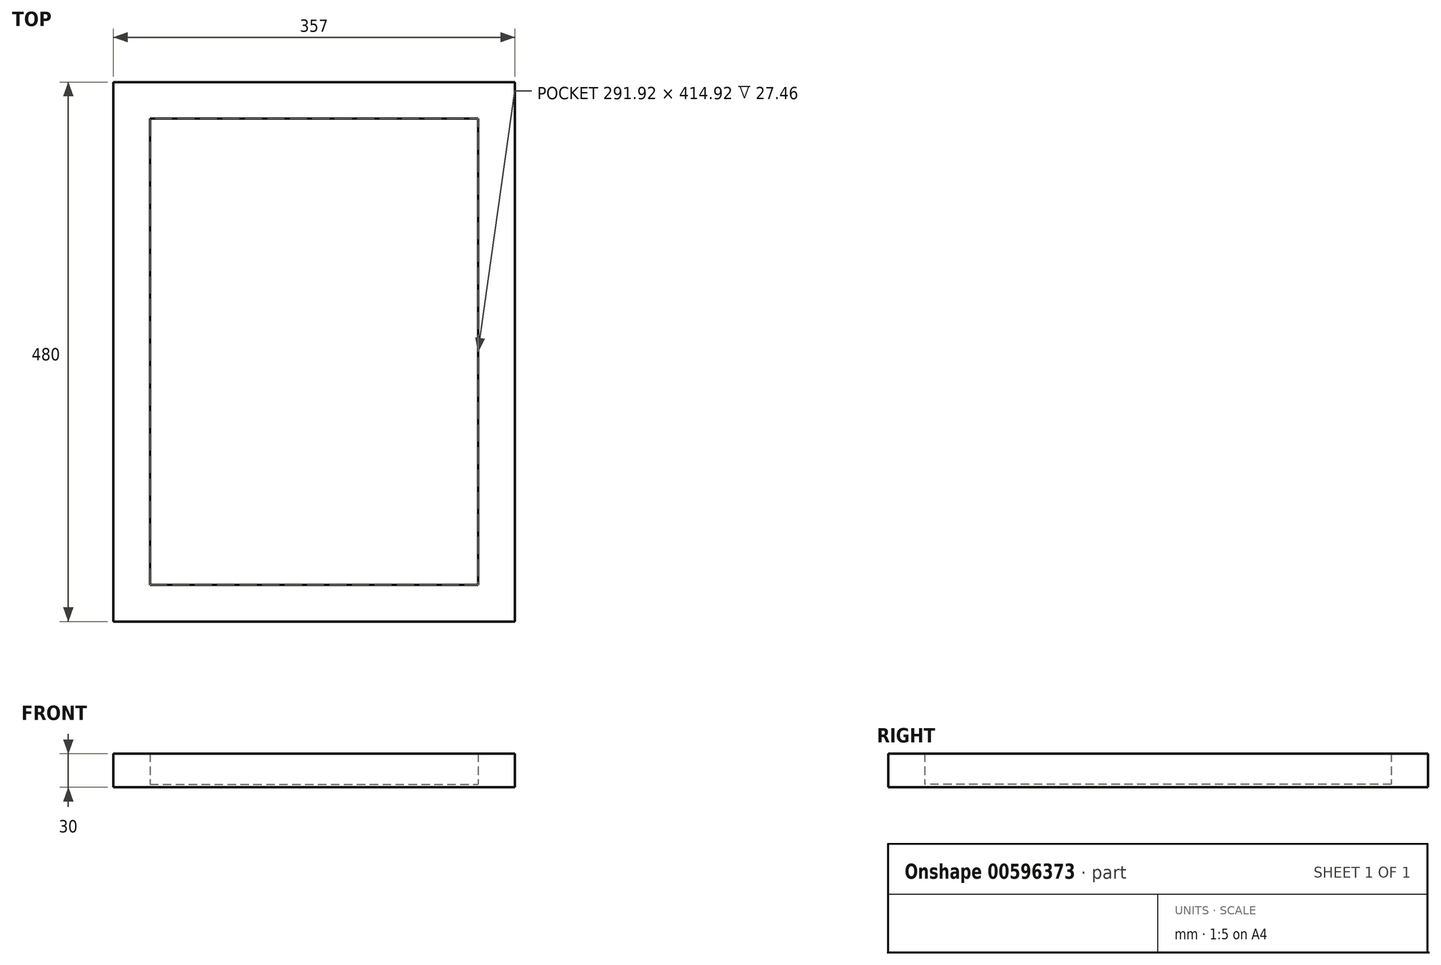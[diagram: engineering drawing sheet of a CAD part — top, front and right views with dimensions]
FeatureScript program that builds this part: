
annotation { "Feature Type Name" : "Feature", "Feature Type Description" : "" }
export const myFeature = defineFeature(function(context is Context, id is Id, definition is map)
    precondition{}
    {
        {
            var Q0;
            Q0=qCreatedBy(makeId("Top.planeOp"),FACE);
            var sketch = newSketch(context, id + "F0", { "sketchPlane" : qUnion([Q0])});
            skLineSegment(sketch, "E0.bottom", {"start": v(-178.5, 240) * mm, "end": v(178.5, 240) * mm});
            skLineSegment(sketch, "E0.top", {"start": v(-178.5, -240) * mm, "end": v(178.5, -240) * mm});
            skLineSegment(sketch, "E0.left", {"start": v(-178.5, 240) * mm, "end": v(-178.5, -240) * mm});
            skLineSegment(sketch, "E0.right", {"start": v(178.5, 240) * mm, "end": v(178.5, -240) * mm});
            skPoint(sketch, "E0.middle", {"position": v(0, 0) * mm});
            skSolve(sketch);
        }
        {
            var Q0;
            Q0=makeQuery(id+"F0.imprint","IMPRINT",FACE,{"disambiguationData":[TD([[makeQuery(id+"F0.imprint","IMPRINT",EDGE,{"derivedFrom":sQuery(id+"F0.wireOp",EDGE,"E0.bottom")}),-1.0]])]});
            extrude(context, id + "F1", {"entities" : qUnion([Q0]), "depth" : 30 * mm, "offsetDistance" : 25.4 * mm});
        }
        {
            var Q0;
            Q0=makeQuery(id+"F1.opExtrude","CAP_FACE",FACE,{"disambiguationData":[OSD([sQuery(id+"F0.wireOp",EDGE,"E0.bottom"),sQuery(id+"F0.wireOp",EDGE,"E0.top"),sQuery(id+"F0.wireOp",EDGE,"E0.left"),sQuery(id+"F0.wireOp",EDGE,"E0.right")])],"isStart":false});
            shell(context, id + "F2", {"entities" : qUnion([Q0]), "thickness" : 2.54 * mm});
        }
        {
            var Q0;
            Q0=makeQuery(id+"F2.opShell","OFFSET_FACE",FACE,{"disambiguationData":[OSD([sQuery(id+"F0.wireOp",EDGE,"E0.bottom")])]});
            extrude(context, id + "F3", {"entities" : qUnion([Q0]), "operationType" : NewBodyOperationType.ADD, "depth" : 30 * mm, "offsetDistance" : 25.4 * mm});
        }
        {
            var Q0;
            Q0=makeQuery(id+"F2.opShell","OFFSET_FACE",FACE,{"disambiguationData":[OSD([sQuery(id+"F0.wireOp",EDGE,"E0.right")])]});
            extrude(context, id + "F4", {"entities" : qUnion([Q0]), "operationType" : NewBodyOperationType.ADD, "depth" : 30 * mm, "offsetDistance" : 25.4 * mm});
        }
        {
            var Q0;
            Q0=makeQuery(id+"F2.opShell","OFFSET_FACE",FACE,{"disambiguationData":[OSD([sQuery(id+"F0.wireOp",EDGE,"E0.left")])]});
            extrude(context, id + "F5", {"entities" : qUnion([Q0]), "operationType" : NewBodyOperationType.ADD, "depth" : 30 * mm, "offsetDistance" : 25.4 * mm});
        }
        {
            var Q0;
            Q0=makeQuery(id+"F2.opShell","OFFSET_FACE",FACE,{"disambiguationData":[OSD([sQuery(id+"F0.wireOp",EDGE,"E0.top")])]});
            extrude(context, id + "F6", {"entities" : qUnion([Q0]), "operationType" : NewBodyOperationType.ADD, "depth" : 30 * mm, "offsetDistance" : 25.4 * mm});
        }
    });
